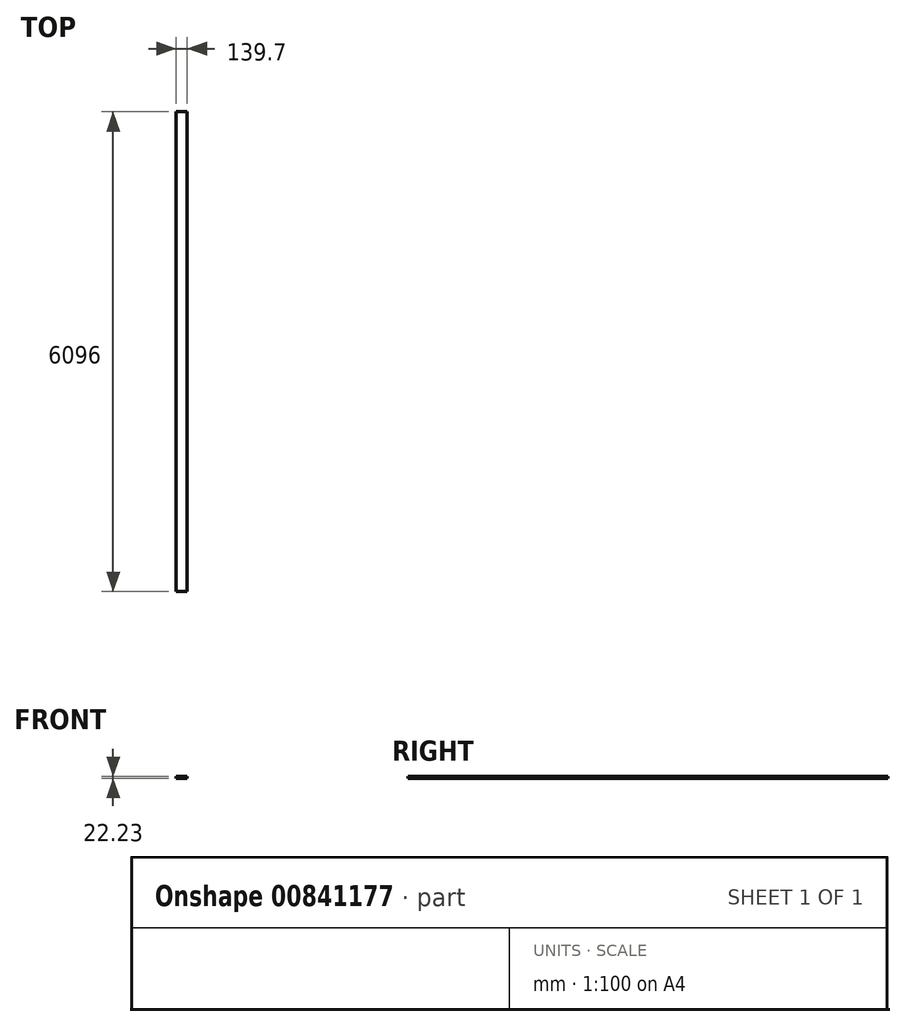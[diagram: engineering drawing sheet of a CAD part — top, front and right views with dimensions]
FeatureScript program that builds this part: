
annotation { "Feature Type Name" : "Feature", "Feature Type Description" : "" }
export const myFeature = defineFeature(function(context is Context, id is Id, definition is map)
    precondition{}
    {
        {
            var Q0;
            Q0=qCreatedBy(makeId("Front.planeOp"),FACE);
            var sketch = newSketch(context, id + "F0", { "sketchPlane" : qUnion([Q0])});
            skLineSegment(sketch, "E0.bottom", {"start": v(0, 0) * mm, "end": v(139.7, 0) * mm});
            skLineSegment(sketch, "E0.top", {"start": v(0, 22.23) * mm, "end": v(139.7, 22.23) * mm});
            skLineSegment(sketch, "E0.left", {"start": v(0, 0) * mm, "end": v(0, 22.23) * mm});
            skLineSegment(sketch, "E0.right", {"start": v(139.7, 0) * mm, "end": v(139.7, 22.23) * mm});
            skSolve(sketch);
        }
        {
            var Q0;
            Q0 = qSketchRegion(id + "F0", true);
            extrude(context, id + "F1", {"entities" : qUnion([Q0]), "depth" : 6096 * mm, "offsetDistance" : 25.4 * mm});
        }
    });
